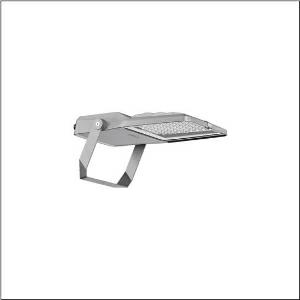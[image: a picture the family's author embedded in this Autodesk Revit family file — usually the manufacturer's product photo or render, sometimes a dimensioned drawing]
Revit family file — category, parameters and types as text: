
# Revit family: floodlight_fl_21_iq_mini___rs12_5xa7772d2b1a_9233
name_source: partatom
category: Lighting Fixtures
units: mm (PartAtom-declared; Revit-internal decimal feet)

## family parameters
Cut with Voids When Loaded = No
Host = Face
Light Source = No
Part Type = Normal
Room Calculation Point = No
Round Connector Dimension = Use Diameter
Shared = No

## types (1)
- --- (1 x LED, 18020 lm, 143 W, 3000K)
    Apparent Load = 143 VA
    CIE Flux Codes = 79 92 99 100 100
    Color Rendering = 70
    Color Temperature = 3000K
    Default Elevation = 1800 mm
    Description = Floodlight FL 21 iQ mini, floodlight, primary light control with lens, of PMMA, primary optical cover: protective disc, of toughened safety glass, transparent, light distribution: RS12, light emission: direct distribution, installation type: surface-mounted, LED, High Power LED, rated luminous flux: 18.020lm, luminous efficacy: 126lm/W, light colour: 730, colour temperature: 3000K, control gear: iQ Street-Remote/DALI, control: Street-Remote, Auto-Match, Temp-Guard, Night-Set, Smart-Wire, Desk-Remote (wireless, voltage-free reading and setting of iQ features in the workshop via application-optimized NFC function/RFID function), optimised constant luminous flux control (CLO 2.0), with terminal, 6-pole, mains connection: 220..240V, AC, 50/60Hz, start of lifetime: 143W, end of service life: 152W, reduction: 61W, luminaire housing, of diecast aluminium, powder-coated, Siteco® metallic grey (DB 702S), corrosivity category C5 mid according to DIN EN ISO 12944, suitable for swimming pools, chlorine-resistant, sealing non-destructively replaceable, mounting bracket, of steel, galvanised, powder-coated, Siteco® metallic grey (DB 702S), protection rating (complete): IP66, insulation class (complete): insulation class II (safety insulation), certification: CE, ENEC, VDE, protection symbol: D, impact resistance: IK08, permissible operating ambient temperature: -40..+40°C, permissible operating ambient temperature for outdoor applications: -40..+50°C, standard: DIN EN 12944, LABS conformity tested according to VDMA 24364:2018-05, packaging unit: 1 piece

Light Distribution: RS12
    Height = 70 mm
    Lamp = 1 x LED
    Lamp Light Flux = 18020 lm
    Lamp Power = 143 W
    Lamp count = 1
    Length = 485 mm
    Luminous efficacy = 126 lm/W
    Manufacturer = Siteco
    ModVariant = No
    Model = 5XA7772D2B1A
    Number of Poles = 1
    OnlyDefault = Yes
    Power Factor = 1
    Product Name = Floodlight FL 21 iQ mini | RS12
    Product group = floodlight | pylon annexe
    ProductGroupID = 6200
    Protection Class = Protection class II
    Protection Degree = IP 66
    RLX_Detail_Level = 1
    RLX_Emergency_Light_Flux = 0 lm
    RLX_Emergency_Type = 0
    RLX_Emergency_Type_DB = No
    RlxData = <blob elided: 91289 chars, md5=27cedca0>
    Socket = socket
    Standby Power = 0 W
    System Light Flux = 18020 lm
    System Power = 143 W
    Type Comments = factory setting: luminous flux: 100 % | dim-lin: 254 | 730 mA
    Type Image = l_1006845.jpg
    URL = http://relux.com
    VarID = @adj_167376
    Voltage = 0 V
    Weight = 0.00 kg
    Width = 337 mm

## geometry (parser evidence)
native form markers: Blend x4, Sweep x14
no freeform markers — native parametric forms only
